# Revit family: О-ВО_Eng
name_source: partatom
category: Duct Accessories
units: mm (PartAtom-declared; Revit-internal decimal feet)

## family parameters
Always vertical = Yes
Cut with Voids When Loaded = No
Part Type = Attaches To
Round Connector Dimension = Use Diameter
Shared = No
Work Plane-Based = No

## types (11) — shared parameters
00_20_Manufacturer = Vents
00_20_Name = Carrier
Casing Material = Metal, painted, blue, matte RAL 5007
Load Classification = HVAC
Maintenance zone material = <By Category>
Manufacturer = Vents
URL = https://ventilation-system.com
d = 8 mm  [stored 0.0262467 ft]
n = 4
zero-valued in all types: Default Elevation

## per-type parameters (varying)
| type | A | A1 | B | B1 | H | Height | Length | M | M1 | R1 | R2 | R3 | R4 | Weight | Width | a |
| O-VO-400 | 510 mm | 500 mm | 395 mm | 385 mm | 115 mm  [stored 0.377297 ft] | 115 mm  [stored 0.377297 ft] | 510 mm | 45 mm  [stored 0.147638 ft] | 40 mm  [stored 0.131234 ft] | 207 mm  [stored 0.679134 ft] | 225 mm  [stored 0.738189 ft] | 289 mm | 64 mm | 1.15 kg | 45 mm  [stored 0.147638 ft] | 160 mm  [stored 0.524934 ft] |
| O-VO-450 | 560 mm | 550 mm | 435 mm | 425 mm | 125 mm  [stored 0.410105 ft] | 125 mm  [stored 0.410105 ft] | 560 mm | 45 mm  [stored 0.147638 ft] | 40 mm  [stored 0.131234 ft] | 232 mm  [stored 0.761155 ft] | 250 mm  [stored 0.82021 ft] | 319 mm | 69 mm | 1.30 kg | 45 mm  [stored 0.147638 ft] | 180 mm  [stored 0.590551 ft] |
| O-VO-500 | 610 mm | 600 mm | 480 mm | 470 mm | 130 mm  [stored 0.426509 ft] | 130 mm  [stored 0.426509 ft] | 610 mm | 45 mm  [stored 0.147638 ft] | 40 mm  [stored 0.131234 ft] | 257 mm  [stored 0.843176 ft] | 280 mm  [stored 0.918635 ft] | 352 mm | 72 mm | 1.40 kg | 45 mm  [stored 0.147638 ft] | 200 mm  [stored 0.656168 ft] |
| O-VO-560 | 670 mm | 660 mm | 525 mm | 515 mm | 140 mm  [stored 0.459318 ft] | 140 mm  [stored 0.459318 ft] | 670 mm | 45 mm  [stored 0.147638 ft] | 40 mm  [stored 0.131234 ft] | 287 mm  [stored 0.941601 ft] | 310 mm  [stored 1.01706 ft] | 388 mm | 78 mm | 1.60 kg | 45 mm  [stored 0.147638 ft] | 230 mm  [stored 0.754593 ft] |
| O-VO-630 | 740 mm | 730 mm | 575 mm | 565 mm | 150 mm | 150 mm | 740 mm | 45 mm  [stored 0.147638 ft] | 40 mm  [stored 0.131234 ft] | 322 mm | 345 mm | 428 mm | 83 mm | 1.80 kg | 45 mm  [stored 0.147638 ft] | 255 mm  [stored 0.836614 ft] |
| O-VO-710 | 820 mm | 810 mm | 630 mm | 620 mm | 160 mm  [stored 0.524934 ft] | 160 mm  [stored 0.524934 ft] | 820 mm | 45 mm  [stored 0.147638 ft] | 40 mm  [stored 0.131234 ft] | 362 mm | 385 mm | 474 mm | 89 mm | 2.00 kg | 45 mm  [stored 0.147638 ft] | 280 mm  [stored 0.918635 ft] |
| O-VO-800 | 910 mm | 900 mm | 705 mm | 695 mm | 180 mm  [stored 0.590551 ft] | 180 mm  [stored 0.590551 ft] | 910 mm | 45 mm  [stored 0.147638 ft] | 40 mm  [stored 0.131234 ft] | 407 mm | 430 mm | 530 mm | 100 mm  [stored 0.328084 ft] | 2.35 kg | 45 mm  [stored 0.147638 ft] | 315 mm  [stored 1.03346 ft] |
| O-VO-900 | 1020 mm | 1010 mm | 795 mm | 785 mm | 215 mm | 215 mm | 1020 mm | 52 mm | 47 mm  [stored 0.154199 ft] | 457 mm | 485 mm | 604 mm | 119 mm | 6.30 kg | 52 mm | 360 mm |
| O-VO-1000 | 1120 mm | 1110 mm | 875 mm | 865 mm | 235 mm  [stored 0.770997 ft] | 235 mm  [stored 0.770997 ft] | 1120 mm | 52 mm | 47 mm  [stored 0.154199 ft] | 507 mm | 535 mm | 666 mm | 131 mm | 7.20 kg | 52 mm | 400 mm |
| O-VO-1120 | 1240 mm | 1230 mm | 1002 mm | 992 mm | 270 mm  [stored 0.885827 ft] | 270 mm  [stored 0.885827 ft] | 1240 mm | 52 mm | 47 mm  [stored 0.154199 ft] | 567 mm | 595 mm | 745 mm | 150 mm | 9.10 kg | 52 mm | 460 mm |
| O-VO-1250 | 1370 mm | 1360 mm | 1087 mm | 1077 mm | 285 mm  [stored 0.935039 ft] | 285 mm  [stored 0.935039 ft] | 1370 mm | 52 mm | 47 mm  [stored 0.154199 ft] | 632 mm | 660 mm | 818 mm | 158 mm | 10.25 kg | 52 mm | 510 mm |

note: column(s) folded — value = type name in every type: 00_20_Type

note: [stored X ft] marks values corroborated as IEEE doubles in the binary element streams (Revit-internal decimal feet)
